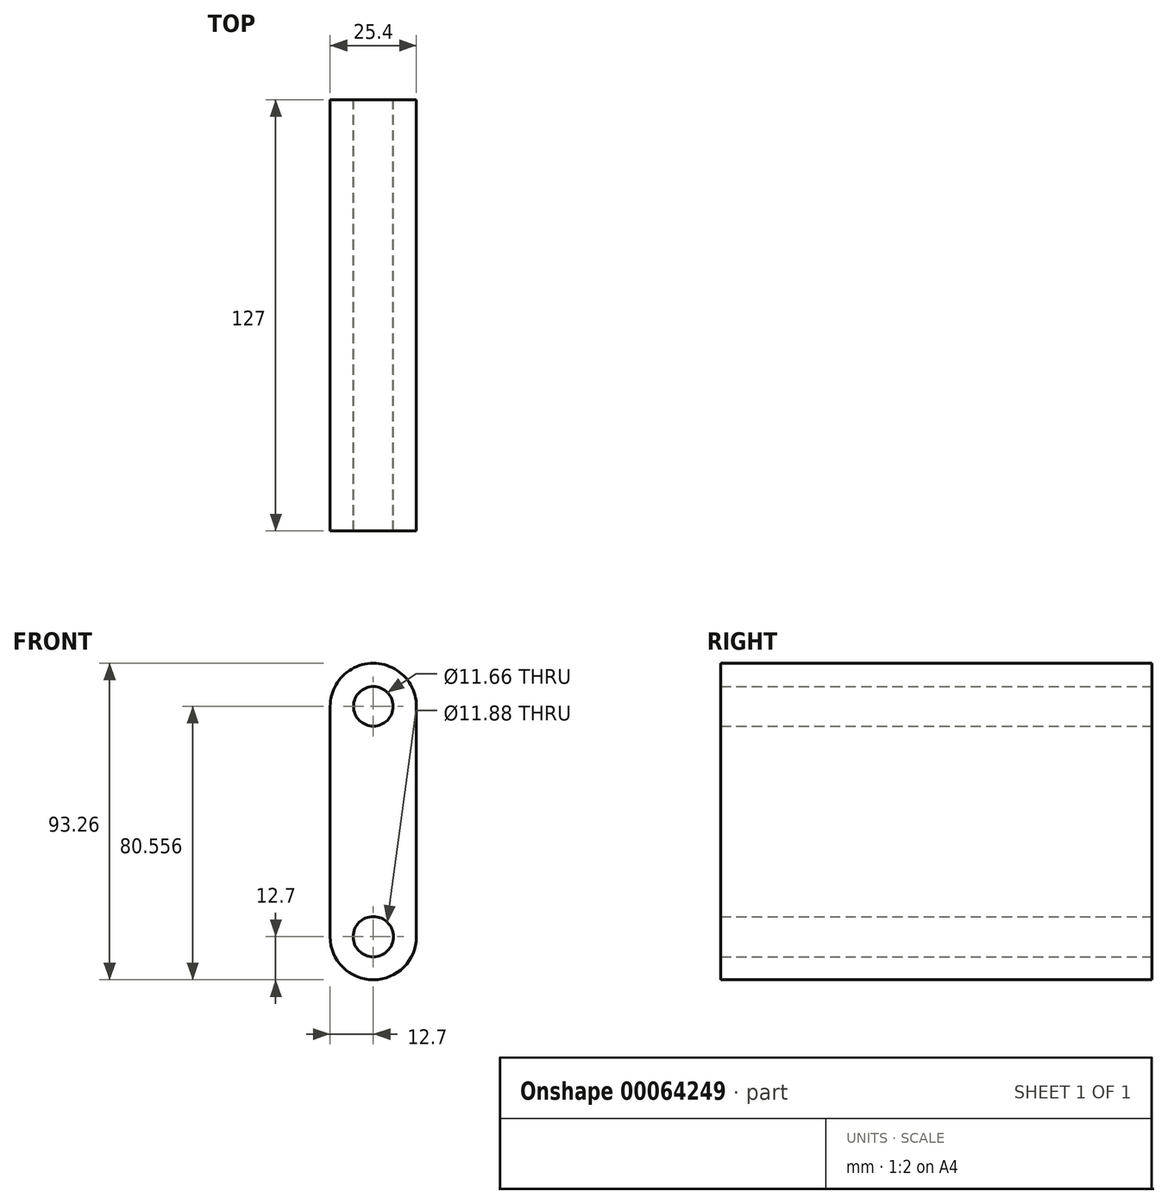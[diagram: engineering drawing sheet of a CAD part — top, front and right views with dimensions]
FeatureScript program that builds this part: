
annotation { "Feature Type Name" : "Feature", "Feature Type Description" : "" }
export const myFeature = defineFeature(function(context is Context, id is Id, definition is map)
    precondition{}
    {
        {
            var Q0;
            Q0=qCreatedBy(makeId("Front.planeOp"),FACE);
            var sketch = newSketch(context, id + "F0", { "sketchPlane" : qUnion([Q0])});
            skLineSegment(sketch, "E0", {"start": v(-12.23, 0) * mm, "end": v(13.17, 0) * mm});
            skLineSegment(sketch, "E1", {"start": v(-12.23, 0) * mm, "end": v(-12.23, 67.83) * mm});
            skLineSegment(sketch, "E2", {"start": v(13.17, 0) * mm, "end": v(13.17, 67.86) * mm});
            skArc(sketch, "E3", {"start": v(-12.23, 0) * mm, "mid": v(0.47, -12.7) * mm, "end": v(13.17, 0) * mm});
            skArc(sketch, "E4", {"start": v(13.17, 67.86) * mm, "mid": v(0.46, 80.56) * mm, "end": v(-12.23, 67.83) * mm});
            skPoint(sketch, "E5.end.orphan", {"position": v(13.17, 67.83) * mm});
            skCircle(sketch, "E6", {"center": v(0.47, 0) * mm, "radius": 5.94 * mm});
            skCircle(sketch, "E7", {"center": v(0.47, 67.86) * mm, "radius": 5.83 * mm});
            skSolve(sketch);
        }
        {
            var Q0;
            {var subQ0=sQuery(id+"F0.wireOp",EDGE,"E0");Q0=makeQuery(id+"F0.imprint","IMPRINT",FACE,{"disambiguationData":[TD([[makeQuery(id+"F0.imprint","IMPRINT",EDGE,{"derivedFrom":subQ0}),1.0]])]});}
            var Q1;
            Q1=makeQuery(id+"F0.imprint","IMPRINT",FACE,{"disambiguationData":[TD([[makeQuery(id+"F0.imprint","IMPRINT",EDGE,{"derivedFrom":sQuery(id+"F0.wireOp",EDGE,"E0")}),-1.0]])]});
            extrude(context, id + "F1", {"entities" : qUnion([Q0, Q1]), "depth" : 127 * mm});
        }
    });
